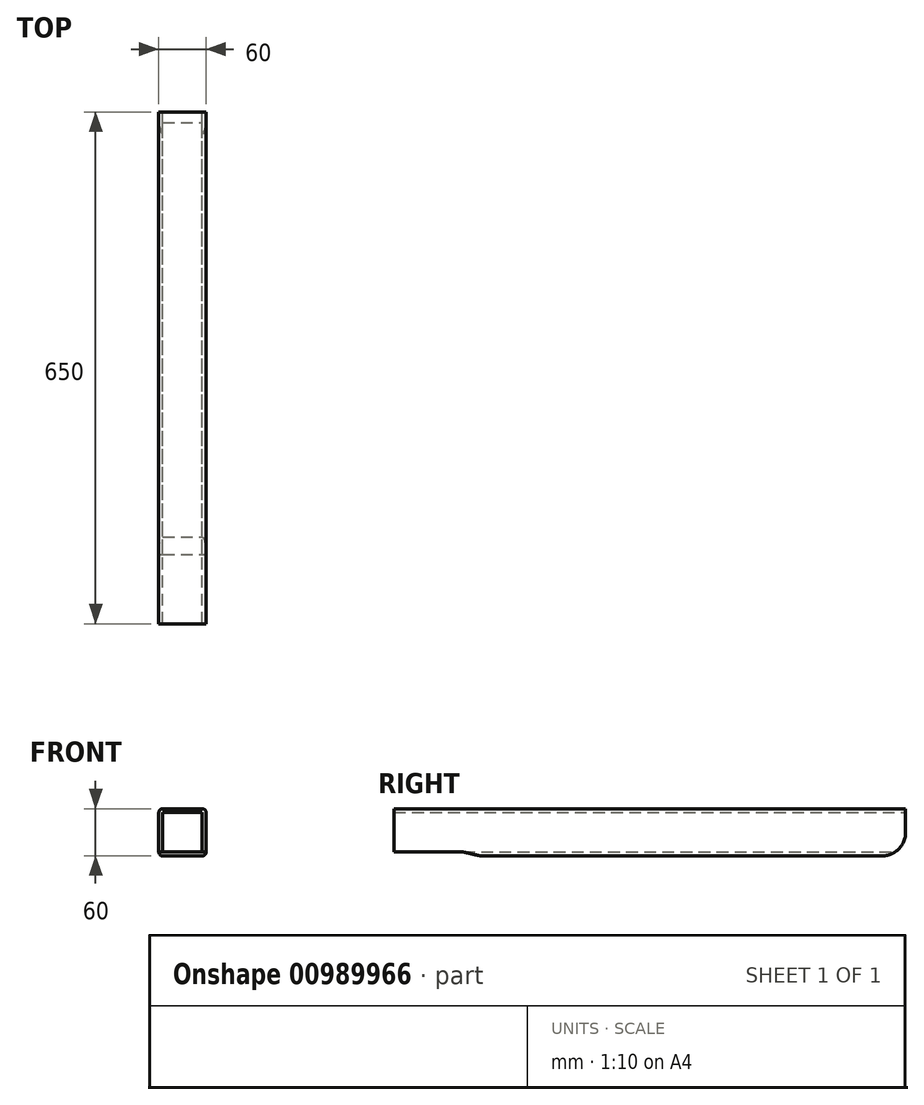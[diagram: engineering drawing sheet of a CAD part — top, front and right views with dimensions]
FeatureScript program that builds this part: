
annotation { "Feature Type Name" : "Feature", "Feature Type Description" : "" }
export const myFeature = defineFeature(function(context is Context, id is Id, definition is map)
    precondition{}
    {
        {
            var Q0;
            Q0=qCreatedBy(makeId("Front.planeOp"),FACE);
            var sketch = newSketch(context, id + "F0", { "sketchPlane" : qUnion([Q0])});
            skLineSegment(sketch, "E0.bottom", {"start": v(25, -30) * mm, "end": v(-25, -30) * mm});
            skLineSegment(sketch, "E0.top", {"start": v(25, 30) * mm, "end": v(-25, 30) * mm});
            skLineSegment(sketch, "E0.left", {"start": v(30, -25) * mm, "end": v(30, 25) * mm});
            skLineSegment(sketch, "E0.right", {"start": v(-30, -25) * mm, "end": v(-30, 25) * mm});
            skPoint(sketch, "E0.middle", {"position": v(0, 0) * mm});
            skPoint(sketch, "E1.visualSharp", {"position": v(-30, 30) * mm});
            skArc(sketch, "E1.filletArc", {"start": v(-25, 30) * mm, "mid": v(-28.54, 28.54) * mm, "end": v(-30, 25) * mm});
            skPoint(sketch, "E2.visualSharp", {"position": v(30, 30) * mm});
            skArc(sketch, "E2.filletArc", {"start": v(30, 25) * mm, "mid": v(28.54, 28.54) * mm, "end": v(25, 30) * mm});
            skPoint(sketch, "E3.visualSharp", {"position": v(30, -30) * mm});
            skArc(sketch, "E3.filletArc", {"start": v(25, -30) * mm, "mid": v(28.54, -28.54) * mm, "end": v(30, -25) * mm});
            skPoint(sketch, "E4.visualSharp", {"position": v(-30, -30) * mm});
            skArc(sketch, "E4.filletArc", {"start": v(-30, -25) * mm, "mid": v(-28.54, -28.54) * mm, "end": v(-25, -30) * mm});
            skLineSegment(sketch, "E5.bottom", {"start": v(25, 25) * mm, "end": v(-25, 25) * mm});
            skLineSegment(sketch, "E5.top", {"start": v(25, -25) * mm, "end": v(-25, -25) * mm});
            skLineSegment(sketch, "E5.left", {"start": v(25, 25) * mm, "end": v(25, -25) * mm});
            skLineSegment(sketch, "E5.right", {"start": v(-25, 25) * mm, "end": v(-25, -25) * mm});
            skSolve(sketch);
        }
        {
            var Q0;
            Q0 = qSketchRegion(id + "F0", true);
            extrude(context, id + "F1", {"entities" : qUnion([Q0]), "endBound" : BoundingType.SYMMETRIC, "depth" : 650 * mm, "offsetDistance" : 25 * mm});
        }
        {
            var Q0;
            Q0=makeQuery(id+"F1.opExtrude","SWEPT_FACE",FACE,{"disambiguationData":[OSD([sQuery(id+"F0.wireOp",EDGE,"E0.left")])]});
            var sketch = newSketch(context, id + "F2", { "sketchPlane" : qUnion([Q0])});
            skLineSegment(sketch, "E6", {"start": v(-347.58, -5) * mm, "end": v(-325, -5) * mm});
            skLineSegment(sketch, "E7", {"start": v(-325, -5) * mm, "end": v(-215, -30) * mm});
            skLineSegment(sketch, "E8", {"start": v(-215, -30) * mm, "end": v(-215, -50.3) * mm});
            skLineSegment(sketch, "E9", {"start": v(-215, -50.3) * mm, "end": v(-354.43, -50.3) * mm});
            skLineSegment(sketch, "E10", {"start": v(-354.43, -50.3) * mm, "end": v(-347.58, -5) * mm});
            skArc(sketch, "E11", {"start": v(295, -30) * mm, "mid": v(316.21, -21.21) * mm, "end": v(325, 0) * mm});
            skLineSegment(sketch, "E12", {"start": v(295, -30) * mm, "end": v(295, -47.22) * mm});
            skLineSegment(sketch, "E13", {"start": v(295, -47.22) * mm, "end": v(357.1, -47.22) * mm});
            skLineSegment(sketch, "E14", {"start": v(357.1, -47.22) * mm, "end": v(357.1, 0) * mm});
            skLineSegment(sketch, "E15", {"start": v(357.1, 0) * mm, "end": v(325, 0) * mm});
            skSolve(sketch);
        }
        {
            var Q0;
            {var subQ7=sQuery(id+"F2.wireOp",EDGE,"E6");Q0=makeQuery(id+"F2.imprint","IMPRINT",FACE,{"disambiguationData":[TD([[makeQuery(id+"F2.imprint","IMPRINT",EDGE,{"derivedFrom":subQ7}),-1.0]])]});}
            var Q1;
            {var subQ0=sQuery(id+"F2.wireOp",EDGE,"518f5754-1eac-4d68-963e-94ce20c885e30.MirrorCS");var subQ1=sQuery(id+"F0.wireOp",EDGE,"E0.left");var subQ2=makeQuery(id+"F1.opExtrude","CAP_EDGE",EDGE,{"disambiguationData":[OSD([subQ1])],"isStart":true});var subQ3=makeQuery(id+"F2.imprint","INTERSECT",VERTEX,{"derivedFrom":[subQ2,sQuery(id+"F2.wireOp",EDGE,"29ba53b6-1430-4853-8f22-bb9ffbb759f70.MirrorCS"),subQ0]});Q1=makeQuery(id+"F2.imprint","IMPRINT",FACE,{"disambiguationData":[TD([[makeQuery(id+"F2.imprint","IMPRINT",EDGE,{"disambiguationData":[TD([[subQ3,-1.0]])],"derivedFrom":subQ0}),1.0]])]});}
            var Q2;
            {var subQ0=sQuery(id+"F2.wireOp",EDGE,"E12");Q2=makeQuery(id+"F2.imprint","IMPRINT",FACE,{"disambiguationData":[TD([[makeQuery(id+"F2.imprint","IMPRINT",EDGE,{"derivedFrom":subQ0}),1.0]])]});}
            var Q3;
            {var subQ0=sQuery(id+"F2.wireOp",EDGE,"E11");var subQ1=sQuery(id+"F0.wireOp",EDGE,"E0.left");var subQ2=makeQuery(id+"F1.opExtrude","CAP_EDGE",EDGE,{"disambiguationData":[OSD([subQ1])],"isStart":true});var subQ3=makeQuery(id+"F2.imprint","INTERSECT",VERTEX,{"derivedFrom":[subQ2,subQ0,sQuery(id+"F2.wireOp",EDGE,"E15")]});Q3=makeQuery(id+"F2.imprint","IMPRINT",FACE,{"disambiguationData":[TD([[makeQuery(id+"F2.imprint","IMPRINT",EDGE,{"disambiguationData":[TD([[subQ3,1.0]])],"derivedFrom":subQ0}),-1.0]])]});}
            extrude(context, id + "F3", {"entities" : qUnion([Q0, Q1, Q2, Q3]), "operationType" : NewBodyOperationType.REMOVE, "endBound" : BoundingType.THROUGH_ALL, "oppositeDirection" : true, "depth" : 25 * mm, "offsetDistance" : 25 * mm});
        }
    });
